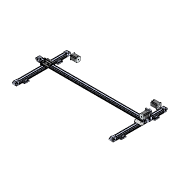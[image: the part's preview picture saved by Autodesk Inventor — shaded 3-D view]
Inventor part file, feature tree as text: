
AUTODESK INVENTOR PART (.ipt)
format: ipt  version: 2020 (Build 240168000, 168)  size: 19,578,368 bytes
history: native  units: mm
features: other x48, sketch x3, projected_geometry x3, extrude x2, hole x1, chamfer x1, fillet x1
ambient origin geometry x8: Origin, YZ Plane, XZ Plane, XY Plane, X Axis, Y Axis, Z Axis, Center Point
bodies: Body1 (feature_tree), Body2 (feature_tree), Body3 (feature_tree), Body4 (feature_tree), Body5 (feature_tree), Body6 (feature_tree), Body7 (feature_tree), Body8 (feature_tree), Body9 (feature_tree), Body10 (feature_tree), Body11 (feature_tree), Body12 (feature_tree), Body13 (feature_tree), Body14 (feature_tree), Body15 (feature_tree), Body16 (feature_tree), Body17 (feature_tree), Body18 (feature_tree), Body19 (feature_tree), Body20 (feature_tree), Body21 (feature_tree), Body22 (feature_tree), Body23 (feature_tree), Body24 (feature_tree)
feature tree (59):
  other  "CCM_Unit.iam"
  other  "CCM_Unit_C.iam:1::RAIL W40-06_B.ipt:1"
  other  "CCM_Unit_C.iam:1::TAILSTOCK W40-00_0+0.ipt:1"
  other  "CCM_Unit_C.iam:1::CART HK32-06W-00__1.ipt:1"
  other  "CCM_Unit_C.iam:1::TAILSTOCK W40-00_0+22_1.ipt:1"
  other  "CCM_Unit_A.iam:1::RAIL W40-06.ipt:1"
  other  "CCM_Unit_A.iam:1::TAILSTOCK W40-00_0+0.ipt:1"
  other  "CCM_Unit_A.iam:1::TAILSTOCK W40-00_22+0_1.ipt:1"
  other  "CCM_Unit_A.iam:1::CART HK32-06W-00__1.ipt:1"
  other  "CCM_Unit_A.iam:1::40 RAIL MOUNT__1.ipt:1"
  other  "CCM_Unit_A.iam:1::40 RAIL MOUNT__1.ipt:2"
  other  "CCM_Unit_B.iam:1::RAIL W40-06.ipt:1"
  other  "CCM_Unit_B.iam:1::TAILSTOCK W40-00_0+0.ipt:1"
  other  "CCM_Unit_B.iam:1::CART HK32-06W-00__1.ipt:1"
  other  "CCM_Unit_B.iam:1::TAILSTOCK W40-00_0+22_1.ipt:1"
  other  "CCM_Unit_B.iam:1::40 RAIL MOUNT__1.ipt:1"
  other  "CCM_Unit_B.iam:1::40 RAIL MOUNT__1.ipt:2"
  other  "CCM_Mount_A.ipt:2"
  other  "57 Aside Speed Reducer(2050)__1.ipt:1"
  other  "NEMA23 Stepper.ipt:1"
  other  "NEMA23 Stepper.ipt:2"
  other  "NEMA23 Stepper.ipt:3"
  other  "CCM_Mount_B.ipt:1"
  other  "OMRON SS-5GL .ipt:1"
  other  "ソリッド1"
  extrude  "押し出し1"  Depth=10.0mm
  hole  "穴1"  [1 undecoded]
  chamfer  "面取り1"  Distance=25.0mm
  extrude  "押し出し2"  Depth=10.0mm TaperAngle=0.0deg
  fillet  "フィレット1"  Radius=2.7mm
  other  "ソリッド2"
  other  "ソリッド3"
  other  "ソリッド4"
  other  "ソリッド5"
  other  "ソリッド6"
  other  "ソリッド7"
  other  "ソリッド8"
  other  "ソリッド9"
  other  "ソリッド10"
  other  "ソリッド11"
  other  "ソリッド12"
  other  "ソリッド13"
  other  "ソリッド14"
  other  "ソリッド15"
  other  "ソリッド16"
  other  "ソリッド17"
  other  "ソリッド18"
  other  "ソリッド19"
  other  "ソリッド20"
  other  "ソリッド21"
  other  "ソリッド22"
  other  "ソリッド25"
  sketch  "スケッチ1"
  projected_geometry  "投影ループ1"
  other  "ソリッド26"
  sketch  "スケッチ2"
  projected_geometry  "投影ループ2"
  sketch  "スケッチ3"
  projected_geometry  "投影ループ3"
note: 1 required parameter value undecoded (feature->parameter linkage not recoverable at this tier; creation-order binding heuristic only, values carry confidence <= 0.55)
